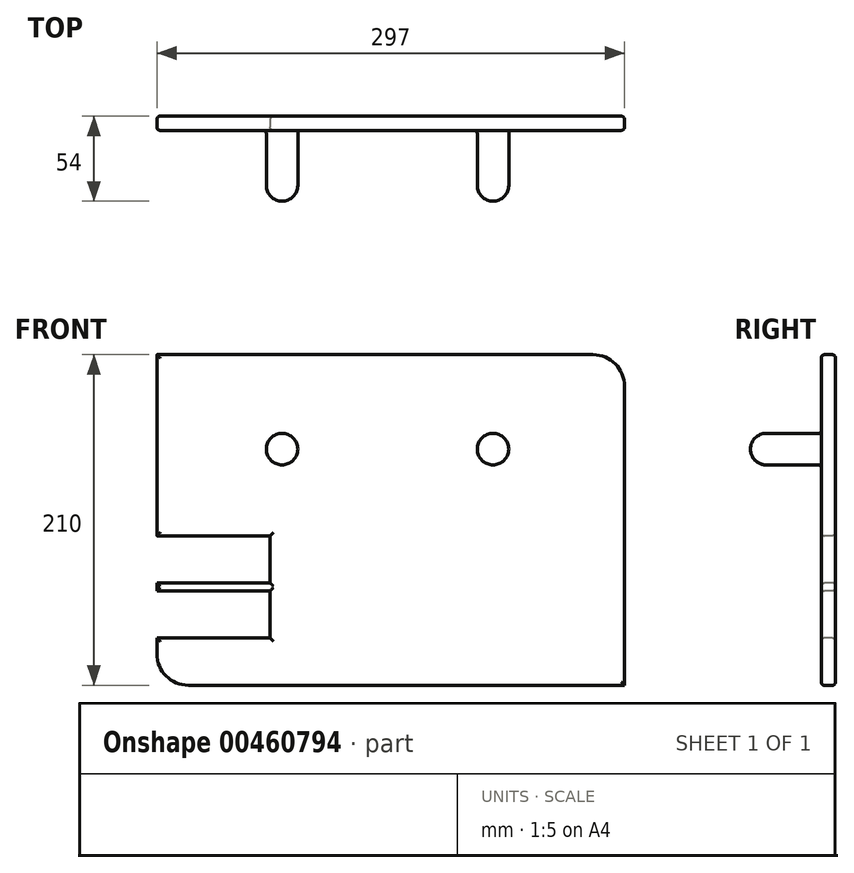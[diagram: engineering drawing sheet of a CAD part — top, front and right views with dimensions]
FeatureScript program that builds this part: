
annotation { "Feature Type Name" : "Feature", "Feature Type Description" : "" }
export const myFeature = defineFeature(function(context is Context, id is Id, definition is map)
    precondition{}
    {
        {
            var Q0;
            Q0=qCreatedBy(makeId("Front.planeOp"),FACE);
            var sketch = newSketch(context, id + "F0", { "sketchPlane" : qUnion([Q0])});
            skLineSegment(sketch, "E0.bottom", {"start": v(-153.1, 74.88) * mm, "end": v(123.9, 74.88) * mm});
            skLineSegment(sketch, "E0.top", {"start": v(-133.1, -135.12) * mm, "end": v(143.9, -135.12) * mm});
            skLineSegment(sketch, "E0.left", {"start": v(-153.1, 74.88) * mm, "end": v(-153.1, -115.12) * mm});
            skLineSegment(sketch, "E0.right", {"start": v(143.9, 54.88) * mm, "end": v(143.9, -135.12) * mm});
            skPoint(sketch, "E1.visualSharp", {"position": v(-153.1, 74.88) * mm});
            skLineSegment(sketch, "E1.filletArc", {"start": v(-153.1, 74.88) * mm, "end": v(-153.1, 74.88) * mm});
            skPoint(sketch, "E2.visualSharp", {"position": v(143.9, -135.12) * mm});
            skLineSegment(sketch, "E2.filletArc", {"start": v(143.9, -135.12) * mm, "end": v(143.9, -135.12) * mm});
            skPoint(sketch, "E3.visualSharp", {"position": v(143.9, 74.88) * mm});
            skArc(sketch, "E3.filletArc", {"start": v(143.9, 54.88) * mm, "mid": v(138.03, 69.03) * mm, "end": v(123.9, 74.88) * mm});
            skPoint(sketch, "E4.visualSharp", {"position": v(-153.1, -135.12) * mm});
            skArc(sketch, "E4.filletArc", {"start": v(-153.1, -115.12) * mm, "mid": v(-147.25, -129.26) * mm, "end": v(-133.1, -135.12) * mm});
            skSolve(sketch);
        }
        {
            var Q0;
            Q0=makeQuery(id+"F0.imprint","IMPRINT",FACE,{"disambiguationData":[TD([[makeQuery(id+"F0.imprint","IMPRINT",EDGE,{"derivedFrom":sQuery(id+"F0.wireOp",EDGE,"E0.bottom")}),-1.0]])]});
            extrude(context, id + "F1", {"entities" : qUnion([Q0]), "depth" : 9 * mm});
        }
        {
            var Q0;
            Q0=makeQuery(id+"F1.opExtrude","CAP_FACE",FACE,{"disambiguationData":[OSD([sQuery(id+"F0.wireOp",EDGE,"E0.bottom"),sQuery(id+"F0.wireOp",EDGE,"E0.top"),sQuery(id+"F0.wireOp",EDGE,"E0.left"),sQuery(id+"F0.wireOp",EDGE,"E0.right"),sQuery(id+"F0.wireOp",EDGE,"E1.filletArc"),sQuery(id+"F0.wireOp",EDGE,"E2.filletArc"),sQuery(id+"F0.wireOp",EDGE,"E3.filletArc"),sQuery(id+"F0.wireOp",EDGE,"E4.filletArc")])],"isStart":false});
            var sketch = newSketch(context, id + "F2", { "sketchPlane" : qUnion([Q0])});
            skCircle(sketch, "E5", {"center": v(60.38, 14.88) * mm, "radius": 10 * mm});
            skCircle(sketch, "E6", {"center": v(-73.6, 14.88) * mm, "radius": 10 * mm});
            skSolve(sketch);
        }
        {
            var Q0;
            Q0=makeQuery(id+"F2.imprint","IMPRINT",FACE,{"disambiguationData":[TD([[makeQuery(id+"F2.imprint","IMPRINT",EDGE,{"derivedFrom":sQuery(id+"F2.wireOp",EDGE,"E5")}),1.0]])]});
            var Q1;
            Q1=makeQuery(id+"F2.imprint","IMPRINT",FACE,{"disambiguationData":[TD([[makeQuery(id+"F2.imprint","IMPRINT",EDGE,{"derivedFrom":sQuery(id+"F2.wireOp",EDGE,"E6")}),1.0]])]});
            extrude(context, id + "F3", {"entities" : qUnion([Q0, Q1]), "operationType" : NewBodyOperationType.ADD, "depth" : 45 * mm});
        }
        {
            var Q0;
            Q0=makeQuery(id+"F1.opExtrude","CAP_FACE",FACE,{"disambiguationData":[OSD([sQuery(id+"F0.wireOp",EDGE,"E0.bottom"),sQuery(id+"F0.wireOp",EDGE,"E0.top"),sQuery(id+"F0.wireOp",EDGE,"E0.left"),sQuery(id+"F0.wireOp",EDGE,"E0.right"),sQuery(id+"F0.wireOp",EDGE,"E3.filletArc"),sQuery(id+"F0.wireOp",EDGE,"E4.filletArc")])],"isStart":false});
            var sketch = newSketch(context, id + "F4", { "sketchPlane" : qUnion([Q0])});
            skLineSegment(sketch, "E7.bottom", {"start": v(-166.14, -105.12) * mm, "end": v(-81.14, -105.12) * mm});
            skLineSegment(sketch, "E7.top", {"start": v(-166.14, -75.12) * mm, "end": v(-81.14, -75.12) * mm});
            skLineSegment(sketch, "E7.left", {"start": v(-166.14, -105.12) * mm, "end": v(-166.14, -75.12) * mm});
            skLineSegment(sketch, "E7.right", {"start": v(-81.14, -105.12) * mm, "end": v(-81.14, -75.12) * mm});
            skSolve(sketch);
        }
        {
            var Q0;
            {var subQ0=sQuery(id+"F4.wireOp",EDGE,"E7.right");Q0=makeQuery(id+"F4.imprint","IMPRINT",FACE,{"disambiguationData":[TD([[makeQuery(id+"F4.imprint","IMPRINT",EDGE,{"derivedFrom":subQ0}),1.0]])]});}
            extrude(context, id + "F5", {"entities" : qUnion([Q0]), "operationType" : NewBodyOperationType.REMOVE, "oppositeDirection" : true, "depth" : 25 * mm});
        }
        {
            var Q0;
            Q0=makeQuery(id+"F1.opExtrude","CAP_FACE",FACE,{"disambiguationData":[OSD([sQuery(id+"F0.wireOp",EDGE,"E0.bottom"),sQuery(id+"F0.wireOp",EDGE,"E0.top"),sQuery(id+"F0.wireOp",EDGE,"E0.left"),sQuery(id+"F0.wireOp",EDGE,"E0.right"),sQuery(id+"F0.wireOp",EDGE,"E3.filletArc"),sQuery(id+"F0.wireOp",EDGE,"E4.filletArc")])],"isStart":false});
            var sketch = newSketch(context, id + "F6", { "sketchPlane" : qUnion([Q0])});
            skLineSegment(sketch, "E8.bottom", {"start": v(-162.8, -70.12) * mm, "end": v(-81.14, -70.12) * mm});
            skLineSegment(sketch, "E8.top", {"start": v(-162.8, -40.12) * mm, "end": v(-81.14, -40.12) * mm});
            skLineSegment(sketch, "E8.left", {"start": v(-162.8, -70.12) * mm, "end": v(-162.8, -40.12) * mm});
            skLineSegment(sketch, "E8.right", {"start": v(-81.14, -70.12) * mm, "end": v(-81.14, -40.12) * mm});
            skSolve(sketch);
        }
        {
            var Q0;
            {var subQ0=sQuery(id+"F6.wireOp",EDGE,"E8.right");Q0=makeQuery(id+"F6.imprint","IMPRINT",FACE,{"disambiguationData":[TD([[makeQuery(id+"F6.imprint","IMPRINT",EDGE,{"derivedFrom":subQ0}),1.0]])]});}
            extrude(context, id + "F7", {"entities" : qUnion([Q0]), "operationType" : NewBodyOperationType.REMOVE, "oppositeDirection" : true, "depth" : 25 * mm});
        }
        {
            var Q0;
            Q0=makeQuery(id+"F1.opExtrude","CAP_FACE",FACE,{"disambiguationData":[OSD([sQuery(id+"F0.wireOp",EDGE,"E0.bottom"),sQuery(id+"F0.wireOp",EDGE,"E0.top"),sQuery(id+"F0.wireOp",EDGE,"E0.left"),sQuery(id+"F0.wireOp",EDGE,"E0.right"),sQuery(id+"F0.wireOp",EDGE,"E3.filletArc"),sQuery(id+"F0.wireOp",EDGE,"E4.filletArc")])],"isStart":false});
            fillet(context, id + "F8", {"entities" : qUnion([Q0]), "radius" : 2 * mm, "tangentPropagation" : true, "allowEdgeOverflow" : false});
        }
        {
            var Q0;
            Q0=makeQuery(id+"F1.opExtrude","CAP_FACE",FACE,{"disambiguationData":[OSD([sQuery(id+"F0.wireOp",EDGE,"E0.bottom"),sQuery(id+"F0.wireOp",EDGE,"E0.top"),sQuery(id+"F0.wireOp",EDGE,"E0.left"),sQuery(id+"F0.wireOp",EDGE,"E0.right"),sQuery(id+"F0.wireOp",EDGE,"E3.filletArc"),sQuery(id+"F0.wireOp",EDGE,"E4.filletArc")])],"isStart":true});
            fillet(context, id + "F9", {"entities" : qUnion([Q0]), "radius" : 2 * mm, "tangentPropagation" : true, "allowEdgeOverflow" : false});
        }
        {
            var Q0;
            Q0=makeQuery(id+"F3.opExtrude","CAP_FACE",FACE,{"disambiguationData":[OSD([sQuery(id+"F2.wireOp",EDGE,"E6")])],"isStart":false});
            fillet(context, id + "F10", {"entities" : qUnion([Q0]), "radius" : 10 * mm, "tangentPropagation" : true, "allowEdgeOverflow" : false});
        }
        {
            var Q0;
            Q0=makeQuery(id+"F3.opExtrude","CAP_FACE",FACE,{"disambiguationData":[OSD([sQuery(id+"F2.wireOp",EDGE,"E5")])],"isStart":false});
            fillet(context, id + "F11", {"entities" : qUnion([Q0]), "radius" : 10 * mm, "tangentPropagation" : true, "allowEdgeOverflow" : false});
        }
    });
